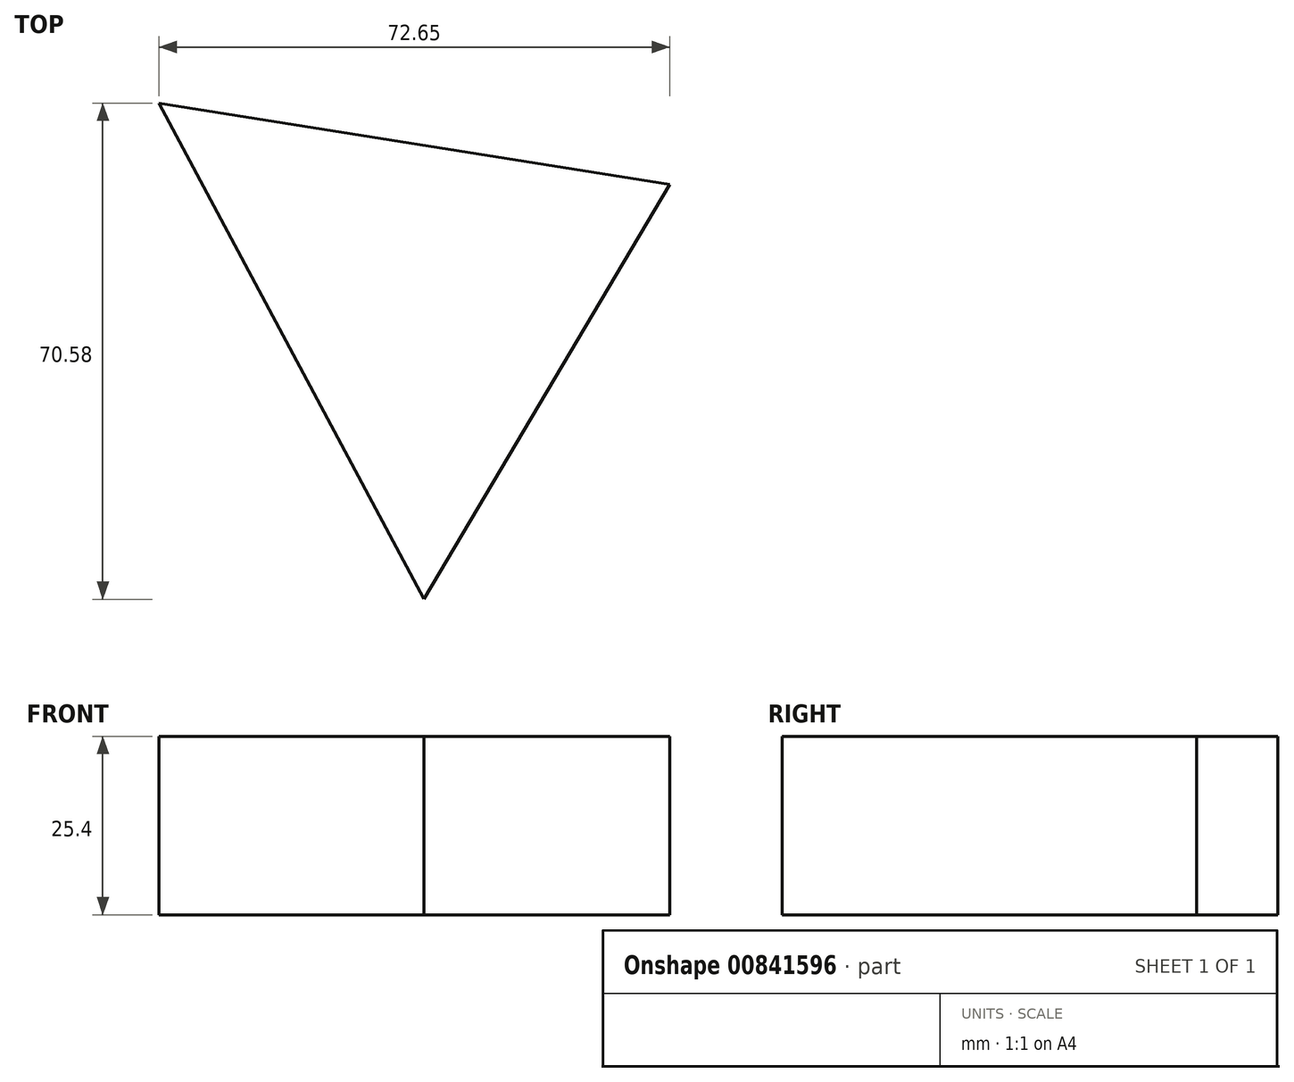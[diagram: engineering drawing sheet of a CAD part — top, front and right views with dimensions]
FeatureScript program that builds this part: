
annotation { "Feature Type Name" : "Feature", "Feature Type Description" : "" }
export const myFeature = defineFeature(function(context is Context, id is Id, definition is map)
    precondition{}
    {
        {
            var Q0;
            Q0=qCreatedBy(makeId("Top.planeOp"),FACE);
            var sketch = newSketch(context, id + "F0", { "sketchPlane" : qUnion([Q0])});
            skLineSegment(sketch, "E0", {"start": v(49.05, 0) * mm, "end": v(9.4, -66.89) * mm});
            skLineSegment(sketch, "E1", {"start": v(9.4, -66.89) * mm, "end": v(-28.25, 3.69) * mm});
            skLineSegment(sketch, "E2", {"start": v(-28.25, 3.69) * mm, "end": v(51.26, -8.93) * mm});
            skLineSegment(sketch, "E3", {"start": v(51.26, -8.93) * mm, "end": v(43.4, 12.92) * mm});
            skLineSegment(sketch, "E4", {"start": v(48.97, -2.59) * mm, "end": v(-28.25, 3.69) * mm});
            skSolve(sketch);
        }
        {
            var Q0;
            {var subQ0=sQuery(id+"F0.wireOp",EDGE,"E1");Q0=makeQuery(id+"F0.imprint","IMPRINT",FACE,{"disambiguationData":[TD([[makeQuery(id+"F0.imprint","IMPRINT",EDGE,{"derivedFrom":subQ0}),-1.0]])]});}
            extrude(context, id + "F1", {"entities" : qUnion([Q0]), "depth" : 25.4 * mm, "offsetDistance" : 25.4 * mm});
        }
    });
